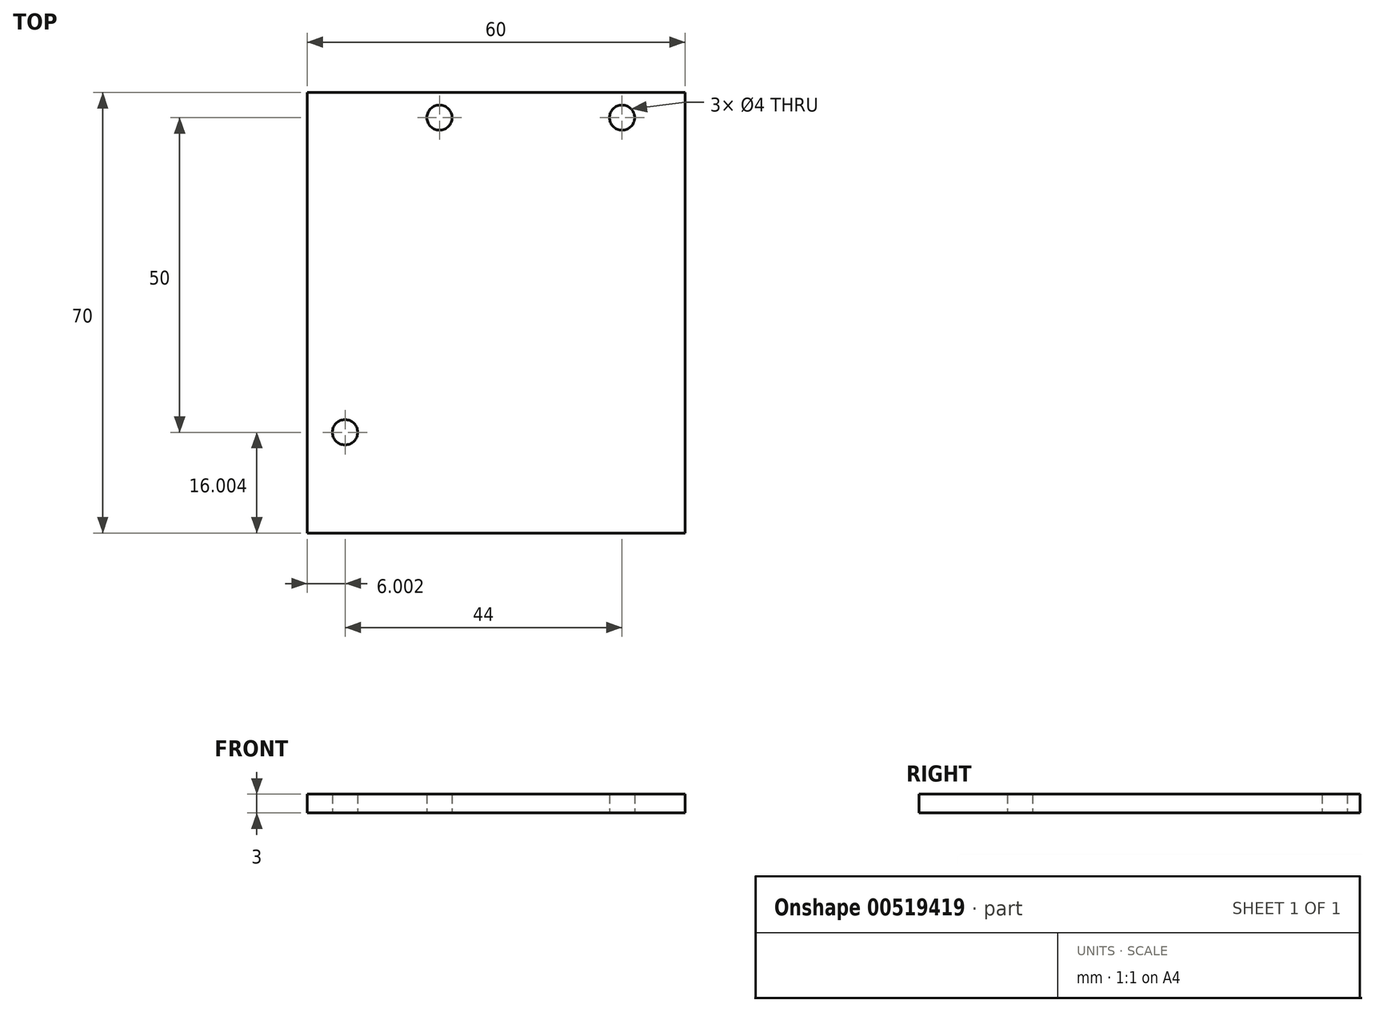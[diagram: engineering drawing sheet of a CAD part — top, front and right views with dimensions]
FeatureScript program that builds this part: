
annotation { "Feature Type Name" : "Feature", "Feature Type Description" : "" }
export const myFeature = defineFeature(function(context is Context, id is Id, definition is map)
    precondition{}
    {
        {
            var Q0;
            Q0=qCreatedBy(makeId("Top.planeOp"),FACE);
            var sketch = newSketch(context, id + "F0", { "sketchPlane" : qUnion([Q0])});
            skLineSegment(sketch, "E0.bottom", {"start": v(-33.06, 51.8) * mm, "end": v(26.94, 51.8) * mm});
            skLineSegment(sketch, "E0.top", {"start": v(-33.06, -18.2) * mm, "end": v(26.94, -18.2) * mm});
            skLineSegment(sketch, "E0.left", {"start": v(-33.06, 51.8) * mm, "end": v(-33.06, -18.2) * mm});
            skLineSegment(sketch, "E0.right", {"start": v(26.94, 51.8) * mm, "end": v(26.94, -18.2) * mm});
            skLineSegment(sketch, "E1.bottom", {"start": v(-30.06, 50.8) * mm, "end": v(23.94, 50.8) * mm});
            skLineSegment(sketch, "E1.top", {"start": v(-30.06, -17.2) * mm, "end": v(23.94, -17.2) * mm});
            skLineSegment(sketch, "E1.left", {"start": v(-30.06, 50.8) * mm, "end": v(-30.06, -17.2) * mm});
            skLineSegment(sketch, "E1.right", {"start": v(23.94, 50.8) * mm, "end": v(23.94, -17.2) * mm});
            skCircle(sketch, "E2", {"center": v(-27.06, -2.2) * mm, "radius": 2 * mm});
            skCircle(sketch, "E3", {"center": v(-12.06, 47.8) * mm, "radius": 2 * mm});
            skCircle(sketch, "E4", {"center": v(16.94, 47.8) * mm, "radius": 2 * mm});
            skSolve(sketch);
        }
        {
            var Q0;
            Q0 = qSketchRegion(id + "F0", true);
            extrude(context, id + "F1", {"entities" : qUnion([Q0]), "depth" : 3 * mm, "offsetDistance" : 25.4 * mm});
        }
        {
            var Q0;
            Q0=makeQuery(id+"F0.imprint","IMPRINT",FACE,{"disambiguationData":[TD([[makeQuery(id+"F0.imprint","IMPRINT",EDGE,{"derivedFrom":sQuery(id+"F0.wireOp",EDGE,"E1.bottom")}),-1.0]])]});
            extrude(context, id + "F2", {"entities" : qUnion([Q0]), "operationType" : NewBodyOperationType.ADD, "depth" : 3 * mm, "offsetDistance" : 25.4 * mm});
        }
    });
